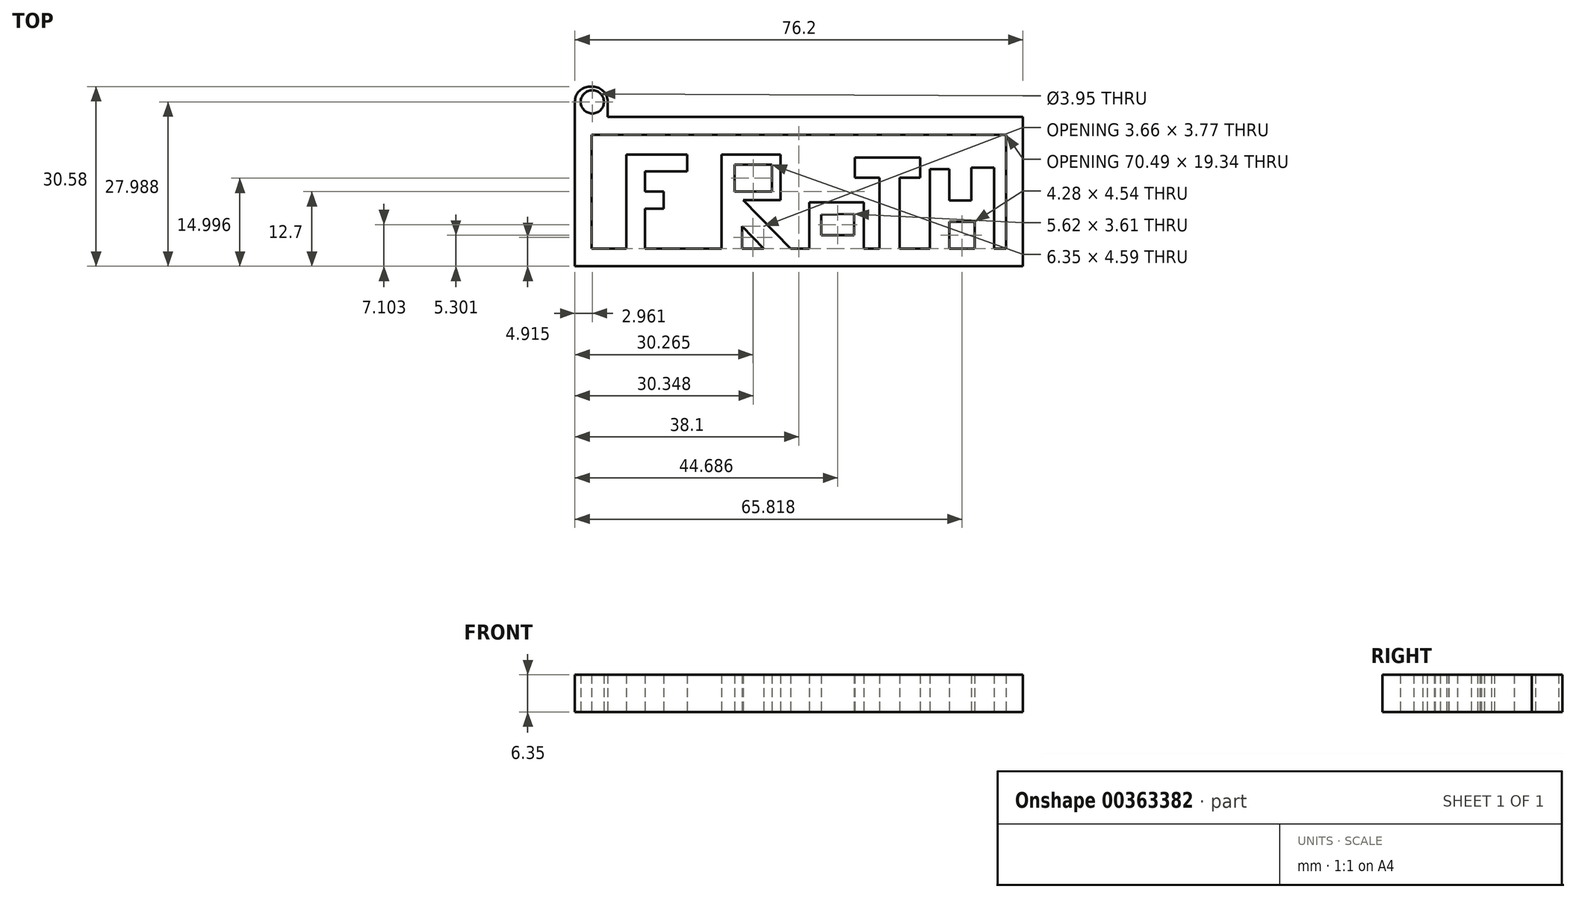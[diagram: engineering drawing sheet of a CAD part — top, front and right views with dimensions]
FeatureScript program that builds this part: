
annotation { "Feature Type Name" : "Feature", "Feature Type Description" : "" }
export const myFeature = defineFeature(function(context is Context, id is Id, definition is map)
    precondition{}
    {
        {
            var Q0;
            Q0=qCreatedBy(makeId("Top.planeOp"),FACE);
            var sketch = newSketch(context, id + "F0", { "sketchPlane" : qUnion([Q0])});
            skLineSegment(sketch, "E0.bottom", {"start": v(38.1, 12.7) * mm, "end": v(-38.1, 12.7) * mm});
            skLineSegment(sketch, "E0.top", {"start": v(38.1, -12.7) * mm, "end": v(-38.1, -12.7) * mm});
            skLineSegment(sketch, "E0.left", {"start": v(38.1, 12.7) * mm, "end": v(38.1, -12.7) * mm});
            skLineSegment(sketch, "E0.right", {"start": v(-38.1, 12.7) * mm, "end": v(-38.1, -12.7) * mm});
            skPoint(sketch, "E0.middle", {"position": v(0, 0) * mm});
            skLineSegment(sketch, "E1.bottom", {"start": v(35.25, 9.67) * mm, "end": v(-35.25, 9.67) * mm});
            skLineSegment(sketch, "E1.top", {"start": v(35.25, -9.67) * mm, "end": v(33.2, -9.67) * mm});
            skLineSegment(sketch, "E1.left", {"start": v(35.25, 9.67) * mm, "end": v(35.25, -9.67) * mm});
            skLineSegment(sketch, "E1.right", {"start": v(-35.25, 9.67) * mm, "end": v(-35.25, -9.67) * mm});
            skLineSegment(sketch, "E2", {"start": v(-29.33, -9.67) * mm, "end": v(-29.33, 6.34) * mm});
            skLineSegment(sketch, "E3", {"start": v(-29.33, 6.34) * mm, "end": v(-19.02, 6.34) * mm});
            skLineSegment(sketch, "E4", {"start": v(-19.02, 6.34) * mm, "end": v(-19.02, 3.48) * mm});
            skLineSegment(sketch, "E5", {"start": v(-19.02, 3.48) * mm, "end": v(-26.16, 3.48) * mm});
            skLineSegment(sketch, "E6", {"start": v(-26.16, 3.48) * mm, "end": v(-26.16, 0) * mm});
            skLineSegment(sketch, "E7", {"start": v(-26.16, 0) * mm, "end": v(-22.98, 0) * mm});
            skLineSegment(sketch, "E8", {"start": v(-22.98, 0) * mm, "end": v(-22.98, -2.87) * mm});
            skLineSegment(sketch, "E9", {"start": v(-22.98, -2.87) * mm, "end": v(-26.16, -2.87) * mm});
            skLineSegment(sketch, "E10", {"start": v(-26.16, -2.87) * mm, "end": v(-26.16, -9.67) * mm});
            skLineSegment(sketch, "E11", {"start": v(-13.15, -9.67) * mm, "end": v(-13.15, 6.34) * mm});
            skPoint(sketch, "E11.endSnap0", {"position": v(-24.17, 6.34) * mm});
            skLineSegment(sketch, "E12", {"start": v(-13.15, 6.34) * mm, "end": v(-3.15, 6.34) * mm});
            skLineSegment(sketch, "E13", {"start": v(-3.15, 6.34) * mm, "end": v(-3.15, -1.44) * mm});
            skLineSegment(sketch, "E14", {"start": v(-3.15, -1.44) * mm, "end": v(-9.5, -1.44) * mm});
            skLineSegment(sketch, "E15", {"start": v(-9.5, -1.44) * mm, "end": v(-1.4, -9.67) * mm});
            skLineSegment(sketch, "E16", {"start": v(-6, -9.67) * mm, "end": v(-9.66, -5.9) * mm});
            skLineSegment(sketch, "E17", {"start": v(-9.66, -5.9) * mm, "end": v(-9.66, -9.67) * mm});
            skLineSegment(sketch, "E18", {"start": v(-10.92, 4.6) * mm, "end": v(-10.92, 0) * mm});
            skLineSegment(sketch, "E19", {"start": v(-10.92, 0) * mm, "end": v(-4.58, 0) * mm});
            skLineSegment(sketch, "E20", {"start": v(-4.58, 0) * mm, "end": v(-4.58, 4.6) * mm});
            skLineSegment(sketch, "E21", {"start": v(-10.92, 4.6) * mm, "end": v(-4.58, 4.6) * mm});
            skLineSegment(sketch, "E22", {"start": v(1.77, -9.67) * mm, "end": v(1.77, -1.79) * mm});
            skLineSegment(sketch, "E23", {"start": v(1.77, -1.79) * mm, "end": v(11, -1.79) * mm});
            skLineSegment(sketch, "E24", {"start": v(11, -1.79) * mm, "end": v(11, -9.67) * mm});
            skLineSegment(sketch, "E25", {"start": v(3.78, -3.93) * mm, "end": v(3.78, -7.4) * mm});
            skLineSegment(sketch, "E26", {"start": v(3.78, -7.4) * mm, "end": v(9.4, -7.4) * mm});
            skLineSegment(sketch, "E27", {"start": v(9.4, -7.4) * mm, "end": v(9.4, -3.8) * mm});
            skLineSegment(sketch, "E28", {"start": v(9.4, -3.8) * mm, "end": v(3.78, -3.93) * mm});
            skLineSegment(sketch, "E29", {"start": v(13.67, -9.67) * mm, "end": v(13.67, 2.36) * mm});
            skLineSegment(sketch, "E30", {"start": v(13.67, 2.36) * mm, "end": v(9.53, 2.36) * mm});
            skLineSegment(sketch, "E31", {"start": v(9.53, 2.36) * mm, "end": v(9.53, 5.84) * mm});
            skLineSegment(sketch, "E32", {"start": v(9.53, 5.84) * mm, "end": v(20.63, 5.84) * mm});
            skLineSegment(sketch, "E33", {"start": v(20.63, 5.84) * mm, "end": v(20.63, 2.36) * mm});
            skLineSegment(sketch, "E34", {"start": v(20.63, 2.36) * mm, "end": v(17.15, 2.36) * mm});
            skLineSegment(sketch, "E35", {"start": v(17.15, 2.36) * mm, "end": v(17.15, -9.67) * mm});
            skPoint(sketch, "E36.endSnap0", {"position": v(15.08, 5.84) * mm});
            skLineSegment(sketch, "E37.trimOffspring", {"start": v(13.67, -9.67) * mm, "end": v(11, -9.67) * mm});
            skLineSegment(sketch, "E38.trimOffspring", {"start": v(1.77, -9.67) * mm, "end": v(-9.66, -9.67) * mm});
            skLineSegment(sketch, "E39.trimOffspring", {"start": v(22.23, -9.67) * mm, "end": v(17.15, -9.67) * mm});
            skLineSegment(sketch, "E40", {"start": v(22.23, -9.67) * mm, "end": v(22.23, 3.83) * mm});
            skLineSegment(sketch, "E41", {"start": v(22.23, 3.83) * mm, "end": v(25.58, 3.83) * mm});
            skLineSegment(sketch, "E42", {"start": v(25.58, 3.83) * mm, "end": v(25.58, -1.52) * mm});
            skLineSegment(sketch, "E43", {"start": v(25.58, -1.52) * mm, "end": v(29.32, -1.52) * mm});
            skLineSegment(sketch, "E44", {"start": v(29.32, -1.52) * mm, "end": v(29.32, 4.1) * mm});
            skLineSegment(sketch, "E45", {"start": v(29.32, 4.1) * mm, "end": v(33.2, 4.1) * mm});
            skLineSegment(sketch, "E46", {"start": v(33.2, 4.1) * mm, "end": v(33.2, -9.67) * mm});
            skLineSegment(sketch, "E47", {"start": v(29.86, -9.67) * mm, "end": v(29.86, -5.13) * mm});
            skLineSegment(sketch, "E48", {"start": v(29.86, -5.13) * mm, "end": v(25.58, -5.13) * mm});
            skLineSegment(sketch, "E49", {"start": v(25.58, -5.13) * mm, "end": v(25.58, -9.67) * mm});
            skLineSegment(sketch, "E50", {"start": v(25.58, -9.67) * mm, "end": v(29.86, -9.67) * mm});
            skLineSegment(sketch, "E51.bottom", {"start": v(-38.1, 12.7) * mm, "end": v(-32.53, 12.7) * mm});
            skLineSegment(sketch, "E51.top", {"start": v(-38.1, 17.88) * mm, "end": v(-32.53, 17.88) * mm});
            skLineSegment(sketch, "E51.left", {"start": v(-38.1, 12.7) * mm, "end": v(-38.1, 17.88) * mm});
            skLineSegment(sketch, "E51.right", {"start": v(-32.53, 12.7) * mm, "end": v(-32.53, 17.88) * mm});
            skCircle(sketch, "E52", {"center": v(-35.14, 15.29) * mm, "radius": 1.98 * mm});
            skPoint(sketch, "E53", {"position": v(-32.53, 15.29) * mm});
            skLineSegment(sketch, "E54.trimOffspring", {"start": v(-29.33, -9.67) * mm, "end": v(-35.25, -9.67) * mm});
            skLineSegment(sketch, "E55.trimOffspring", {"start": v(-13.15, -9.67) * mm, "end": v(-26.16, -9.67) * mm});
            skSolve(sketch);
        }
        {
            var Q0;
            Q0 = qSketchRegion(id + "F0", true);
            extrude(context, id + "F1", {"entities" : qUnion([Q0]), "depth" : 6.35 * mm});
        }
        {
            var Q0;
            Q0=makeQuery(id+"F1.opExtrude","SWEPT_EDGE",EDGE,{"disambiguationData":[OSD([sQuery(id+"F0.wireOp",EDGE,"E51.top"),sQuery(id+"F0.wireOp",EDGE,"E51.left")])]});
            var Q1;
            Q1=makeQuery(id+"F1.opExtrude","SWEPT_EDGE",EDGE,{"disambiguationData":[OSD([sQuery(id+"F0.wireOp",EDGE,"E51.top"),sQuery(id+"F0.wireOp",EDGE,"E51.right")])]});
            fillet(context, id + "F2", {"entities" : qUnion([Q0, Q1]), "radius" : 2.54 * mm, "tangentPropagation" : true, "allowEdgeOverflow" : false});
        }
    });
